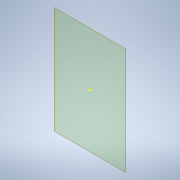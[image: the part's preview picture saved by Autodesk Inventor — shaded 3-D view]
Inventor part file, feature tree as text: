
AUTODESK INVENTOR PART (.ipt)
format: ipt  version: 2022 (Build 260153000, 153)  size: 143,360 bytes
history: native  units: mm
features: other x3, plane x1, extrude x1, sketch x1, reference x1
ambient origin geometry x8: Origin, YZ Plane, XZ Plane, XY Plane, X Axis, Y Axis, Z Axis, Center Point
bodies: Volumenkörper1 (feature_tree)
feature tree (7):
  plane  "Arbeitsebene1"
  extrude  "Extrusion1"  [1 undecoded]
  sketch  "Skizze1"  dims[d0=8.2mm d1=0.0mm]
  reference  "Referenz1"
  other  "Omniscope_new_v0.iam"
  other  "Omniscope_sidewalls_v0:1"
  other  "Omniscope_mid_level_v0:1"
note: 1 required parameter value undecoded (feature->parameter linkage not recoverable at this tier; creation-order binding heuristic only, values carry confidence <= 0.55)
